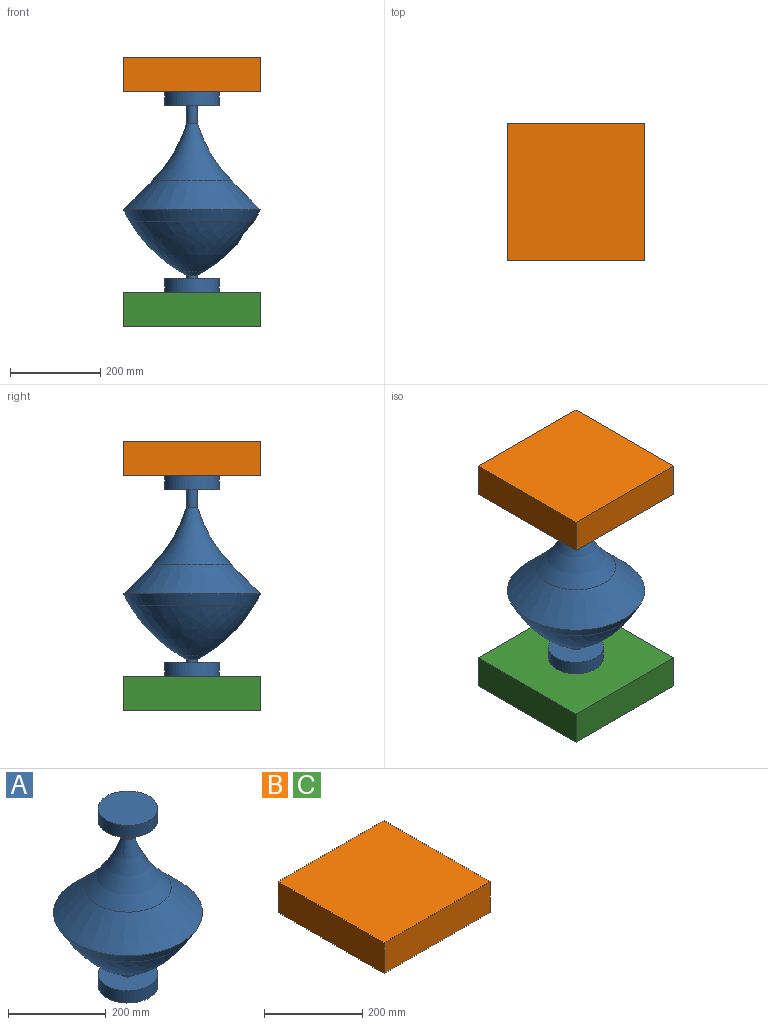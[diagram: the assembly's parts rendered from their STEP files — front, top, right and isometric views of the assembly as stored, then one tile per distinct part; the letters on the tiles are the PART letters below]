
ASSEMBLY  parts=3 mates=2
PART A: 13 faces, bbox 304.8x304.8x444.6 mm
  f0: plane 121.92x121.92mm, normal (0,0,1), area 11674.5mm2, adj f1
  f1: cylinder r=60.96mm len=121.92mm, axis (0,0,-1), area 11674.5mm2, adj f0,f2
  f2: plane 121.92x121.92mm, normal (0,0,-1), area 11209.1mm2, adj f1,f3
  f3: cylinder r=12.17mm len=40.11mm, axis (0,0,-1), area 3067.3mm2, adj f2,f4
  f4: torus R=303.83mm, axis (0,0,-1), area 42314.9mm2, adj f3,f5
  f5: cone r=88.31mm half-angle=45deg, axis (0,0,-1), area 68542.1mm2, adj f4,f6
  f6: cone r=152.4mm half-angle=30deg, axis (0,0,1), area 27221.2mm2, adj f5,f7
  f7: revolved ~274.91x274.91mm, area 86799.4mm2, adj f6,f8
  f8: cone r=25.89mm half-angle=60deg, axis (0,0,1), area 1893.8mm2, adj f7,f9
  f9: cylinder r=12.17mm len=24.35mm, axis (0,0,-1), area 537.5mm2, adj f8,f10
  f10: plane 121.92x121.92mm, normal (0,0,1), area 11209.1mm2, adj f9,f11
  f11: cylinder r=60.96mm len=121.92mm, axis (0,0,-1), area 11674.5mm2, adj f10,f12
  f12: plane 121.92x121.92mm, normal (0,0,-1), area 11674.5mm2, adj f11
PART B: 6 faces, bbox 304.8x304.8x76.2 mm
  f0: plane 304.8x304.8mm, normal (0,0,1), area 92903mm2, adj f1,f3,f4,f5
  f1: plane 304.8x76.2mm, normal (-1,0,0), area 23225.8mm2, adj f0,f2,f4,f5
  f2: plane 304.8x304.8mm, normal (0,0,-1), area 92903mm2, adj f1,f3,f4,f5
  f3: plane 304.8x76.2mm, normal (1,0,0), area 23225.8mm2, adj f0,f2,f4,f5
  f4: plane 304.8x76.2mm, normal (0,-1,0), area 23225.8mm2, adj f0,f1,f2,f3
  f5: plane 304.8x76.2mm, normal (0,1,0), area 23225.8mm2, adj f0,f1,f2,f3
PART C: same geometry as B
PLACE A t=(-6.14,57.02,-12.3)mm
PLACE B t=(116.02,209.42,270.29)mm
PLACE C t=(116.02,209.42,-250.47)mm
MATE fastened C.f0 <-> A.f1  axis (0,0,1) through (-6.14,57.02,-195.18)mm
MATE fastened B.f2 <-> A.f1  axis (0,0,-1) through (-6.14,57.02,249.38)mm
